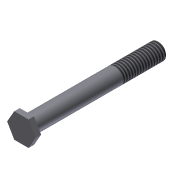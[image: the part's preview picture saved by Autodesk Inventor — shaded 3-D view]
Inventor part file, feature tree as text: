
AUTODESK INVENTOR PART (.ipt)
format: ipt  version: 2013 (Build 170138000, 138)  size: 91,648 bytes
history: native  units: in
note: dims shown in document units (in); Inventor stores cm internally (conversion verified against a paired STEP export)
features: extrude x2, sketch x2, thread x1, chamfer x1
ambient origin geometry x8: Origin, YZ Plane, XZ Plane, XY Plane, X Axis, Y Axis, Z Axis, Center Point
bodies: Solid1 (feature_tree)
feature tree (6):
  extrude  "Extrusion1"  Depth=3.0in TaperAngle=0.0deg
  extrude  "Extrusion2"  Depth=0.125in TaperAngle=0.0deg
  thread  "Thread1"  [1 undecoded]
  chamfer  "Chamfer1"  Distance=0.02in Angle=45.0deg
  sketch  "Sketch1"  dims[d0=0.375in d1=3.0in d2=0.0in]
  sketch  "Sketch2"  dims[d3=0.5625in d4=0.125in d5=0.0in d6=1.0in d7=0.0in d8=0.02in d9=0.125in d10=45.0deg]
note: 1 required parameter value undecoded (feature->parameter linkage not recoverable at this tier; creation-order binding heuristic only, values carry confidence <= 0.55)
